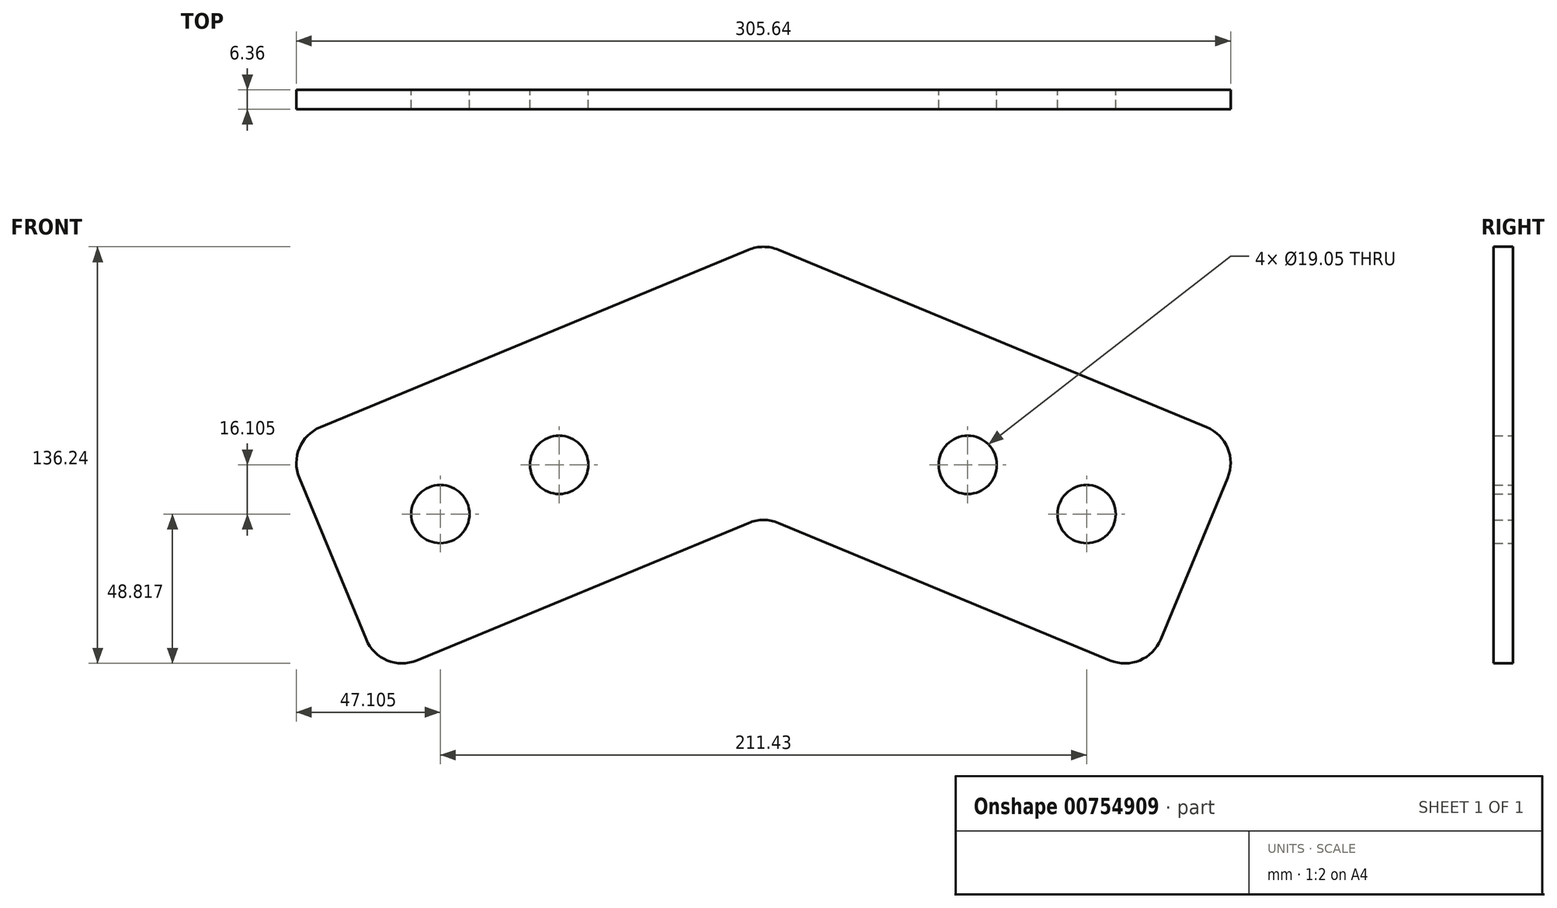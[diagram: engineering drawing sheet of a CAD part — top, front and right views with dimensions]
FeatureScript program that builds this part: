
annotation { "Feature Type Name" : "Feature", "Feature Type Description" : "" }
export const myFeature = defineFeature(function(context is Context, id is Id, definition is map)
    precondition{}
    {
        {
            var Q0;
            Q0=qCreatedBy(makeId("Front.planeOp"),FACE);
            var sketch = newSketch(context, id + "F0", { "sketchPlane" : qUnion([Q0])});
            skLineSegment(sketch, "E0", {"start": v(0, 0) * mm, "end": v(-125.12, -51.83) * mm});
            skLineSegment(sketch, "E1", {"start": v(0, 0) * mm, "end": v(0, 89.35) * mm});
            skLineSegment(sketch, "E2", {"start": v(-125.12, -51.83) * mm, "end": v(-156.71, 24.44) * mm});
            skLineSegment(sketch, "E3", {"start": v(-156.71, 24.44) * mm, "end": v(0, 89.35) * mm});
            skPoint(sketch, "E4", {"position": v(-15.88, 93.09) * mm});
            skPoint(sketch, "E5", {"position": v(-15.88, -16.89) * mm});
            skLineSegment(sketch, "E6.MirrorCS", {"start": v(0, 0) * mm, "end": v(125.12, -51.83) * mm});
            skPoint(sketch, "E7.MirrorP", {"position": v(15.88, -16.89) * mm});
            skLineSegment(sketch, "E8.MirrorCS", {"start": v(125.12, -51.83) * mm, "end": v(156.71, 24.44) * mm});
            skLineSegment(sketch, "E9.MirrorCS", {"start": v(156.71, 24.44) * mm, "end": v(0, 89.35) * mm});
            skPoint(sketch, "E10.MirrorP", {"position": v(15.88, 93.09) * mm});
            skLineSegment(sketch, "E11", {"start": v(-15.88, -16.89) * mm, "end": v(-45.04, 53.51) * mm, "construction": true});
            skLineSegment(sketch, "E12", {"start": v(-15.88, 93.09) * mm, "end": v(13.29, 22.69) * mm, "construction": true});
            skLineSegment(sketch, "E13", {"start": v(-121.51, 39.02) * mm, "end": v(-89.92, -37.25) * mm, "construction": true});
            skPoint(sketch, "E14", {"position": v(-105.71, 0.89) * mm});
            skLineSegment(sketch, "E15", {"start": v(-105.71, 0.89) * mm, "end": v(-35.32, 30.05) * mm, "construction": true});
            skCircle(sketch, "E16", {"center": v(-105.71, 0.89) * mm, "radius": 9.53 * mm});
            skLineSegment(sketch, "E17", {"start": v(-82.63, 55.13) * mm, "end": v(-51.04, -21.14) * mm, "construction": true});
            skLineSegment(sketch, "E18", {"start": v(-51.04, -21.14) * mm, "end": v(-66.83, 17) * mm});
            skLineSegment(sketch, "E19", {"start": v(-66.83, 17) * mm, "end": v(3.57, 46.15) * mm, "construction": true});
            skCircle(sketch, "E20", {"center": v(-66.83, 17) * mm, "radius": 9.53 * mm});
            skCircle(sketch, "E21.MirrorC", {"center": v(66.83, 17) * mm, "radius": 9.53 * mm});
            skCircle(sketch, "E22.MirrorC", {"center": v(105.71, 0.89) * mm, "radius": 9.53 * mm});
            skLineSegment(sketch, "E23", {"start": v(-140.91, -13.7) * mm, "end": v(-105.71, 0.89) * mm, "construction": true});
            skSolve(sketch);
        }
        {
            var Q0;
            Q0=qSketchRegion(id+"F0",true);
            extrude(context, id + "F1", {"entities" : qUnion([Q0]), "endBound" : BoundingType.SYMMETRIC, "depth" : 6.35 * mm, "offsetDistance" : 25.4 * mm});
        }
        {
            var Q0;
            Q0=makeQuery(id+"F1.opExtrude","SWEPT_EDGE",EDGE,{"disambiguationData":[OSD([sQuery(id+"F0.wireOp",EDGE,"E2"),sQuery(id+"F0.wireOp",EDGE,"E3")])]});
            var Q1;
            Q1=makeQuery(id+"F1.opExtrude","SWEPT_EDGE",EDGE,{"disambiguationData":[OSD([sQuery(id+"F0.wireOp",EDGE,"E3"),sQuery(id+"F0.wireOp",EDGE,"E1"),sQuery(id+"F0.wireOp",EDGE,"E9.MirrorCS")])]});
            var Q2;
            Q2=makeQuery(id+"F1.opExtrude","SWEPT_EDGE",EDGE,{"disambiguationData":[OSD([sQuery(id+"F0.wireOp",EDGE,"E0"),sQuery(id+"F0.wireOp",EDGE,"E6.MirrorCS"),sQuery(id+"F0.wireOp",EDGE,"E1")])]});
            var Q3;
            Q3=makeQuery(id+"F1.opExtrude","SWEPT_EDGE",EDGE,{"disambiguationData":[OSD([sQuery(id+"F0.wireOp",EDGE,"E6.MirrorCS"),sQuery(id+"F0.wireOp",EDGE,"E8.MirrorCS")])]});
            var Q4;
            Q4=makeQuery(id+"F1.opExtrude","SWEPT_EDGE",EDGE,{"disambiguationData":[OSD([sQuery(id+"F0.wireOp",EDGE,"E8.MirrorCS"),sQuery(id+"F0.wireOp",EDGE,"E9.MirrorCS")])]});
            var Q5;
            Q5=makeQuery(id+"F1.opExtrude","SWEPT_EDGE",EDGE,{"disambiguationData":[OSD([sQuery(id+"F0.wireOp",EDGE,"E0"),sQuery(id+"F0.wireOp",EDGE,"E2")])]});
            fillet(context, id + "F2", {"entities" : qUnion([Q0, Q1, Q2, Q3, Q4, Q5]), "radius" : 12.7 * mm, "tangentPropagation" : true, "allowEdgeOverflow" : false});
        }
    });
